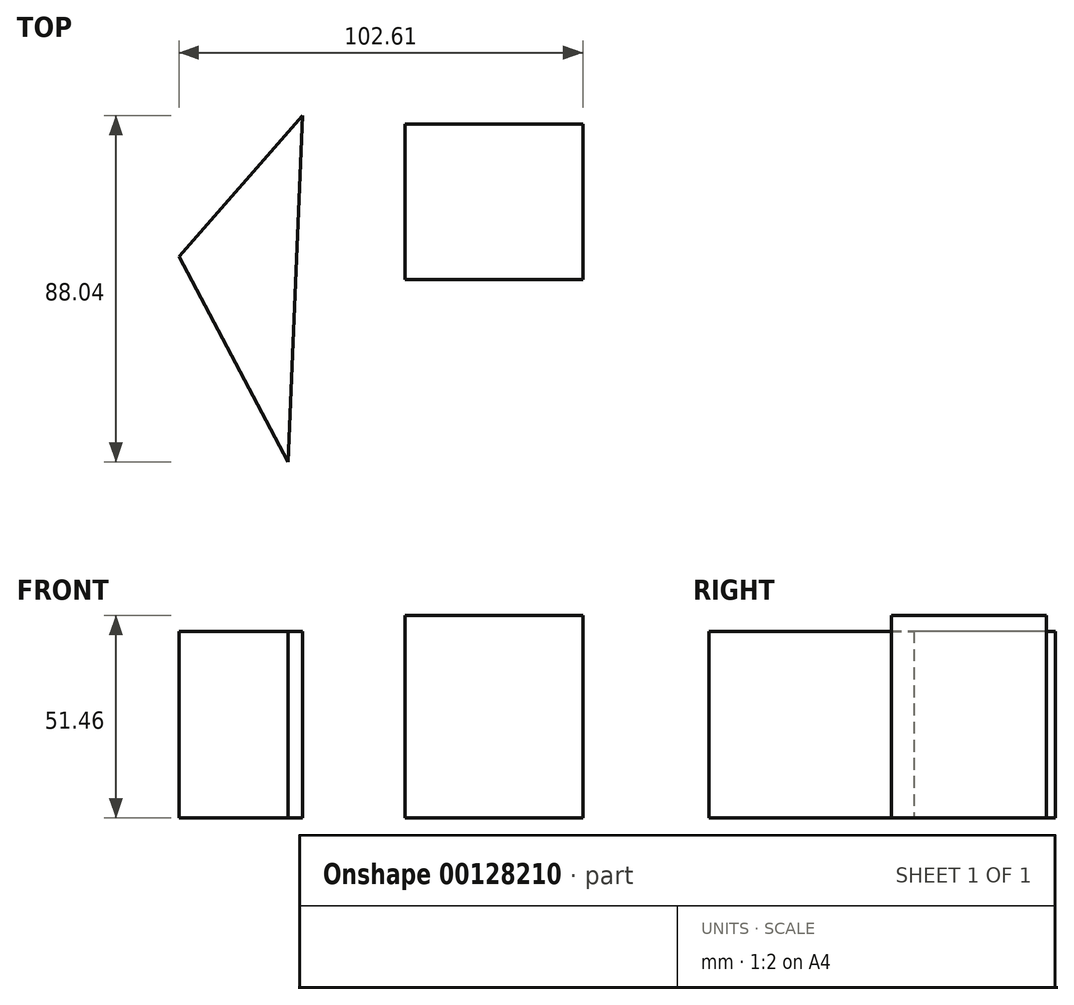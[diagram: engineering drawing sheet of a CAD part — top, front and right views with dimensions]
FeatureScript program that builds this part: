
annotation { "Feature Type Name" : "Feature", "Feature Type Description" : "" }
export const myFeature = defineFeature(function(context is Context, id is Id, definition is map)
    precondition{}
    {
        {
            var Q0;
            Q0=qCreatedBy(makeId("Top.planeOp"),FACE);
            var sketch = newSketch(context, id + "F0", { "sketchPlane" : qUnion([Q0])});
            skLineSegment(sketch, "E0.bottom", {"start": v(0, 39.38) * mm, "end": v(45.15, 39.38) * mm});
            skLineSegment(sketch, "E0.top", {"start": v(0, 0) * mm, "end": v(45.15, 0) * mm});
            skLineSegment(sketch, "E0.left", {"start": v(0, 39.38) * mm, "end": v(0, 0) * mm});
            skLineSegment(sketch, "E0.right", {"start": v(45.15, 39.38) * mm, "end": v(45.15, 0) * mm});
            skSolve(sketch);
        }
        {
            var Q0;
            Q0=qSketchRegion(id+"F0",true);
            extrude(context, id + "F1", {"entities" : qUnion([Q0]), "depth" : 51.46 * mm});
        }
        {
            var Q0;
            Q0=qCreatedBy(makeId("Top.planeOp"),FACE);
            var sketch = newSketch(context, id + "F2", { "sketchPlane" : qUnion([Q0])});
            skLineSegment(sketch, "E1", {"start": v(-26.07, 41.63) * mm, "end": v(-57.46, 5.73) * mm});
            skLineSegment(sketch, "E2", {"start": v(-29.68, -46.41) * mm, "end": v(-57.46, 5.73) * mm});
            skLineSegment(sketch, "E3", {"start": v(-26.07, 41.63) * mm, "end": v(-29.68, -46.41) * mm});
            skSolve(sketch);
        }
        {
            var Q0;
            Q0=qSketchRegion(id+"F2",true);
            extrude(context, id + "F3", {"entities" : qUnion([Q0]), "depth" : 47.46 * mm});
        }
    });
